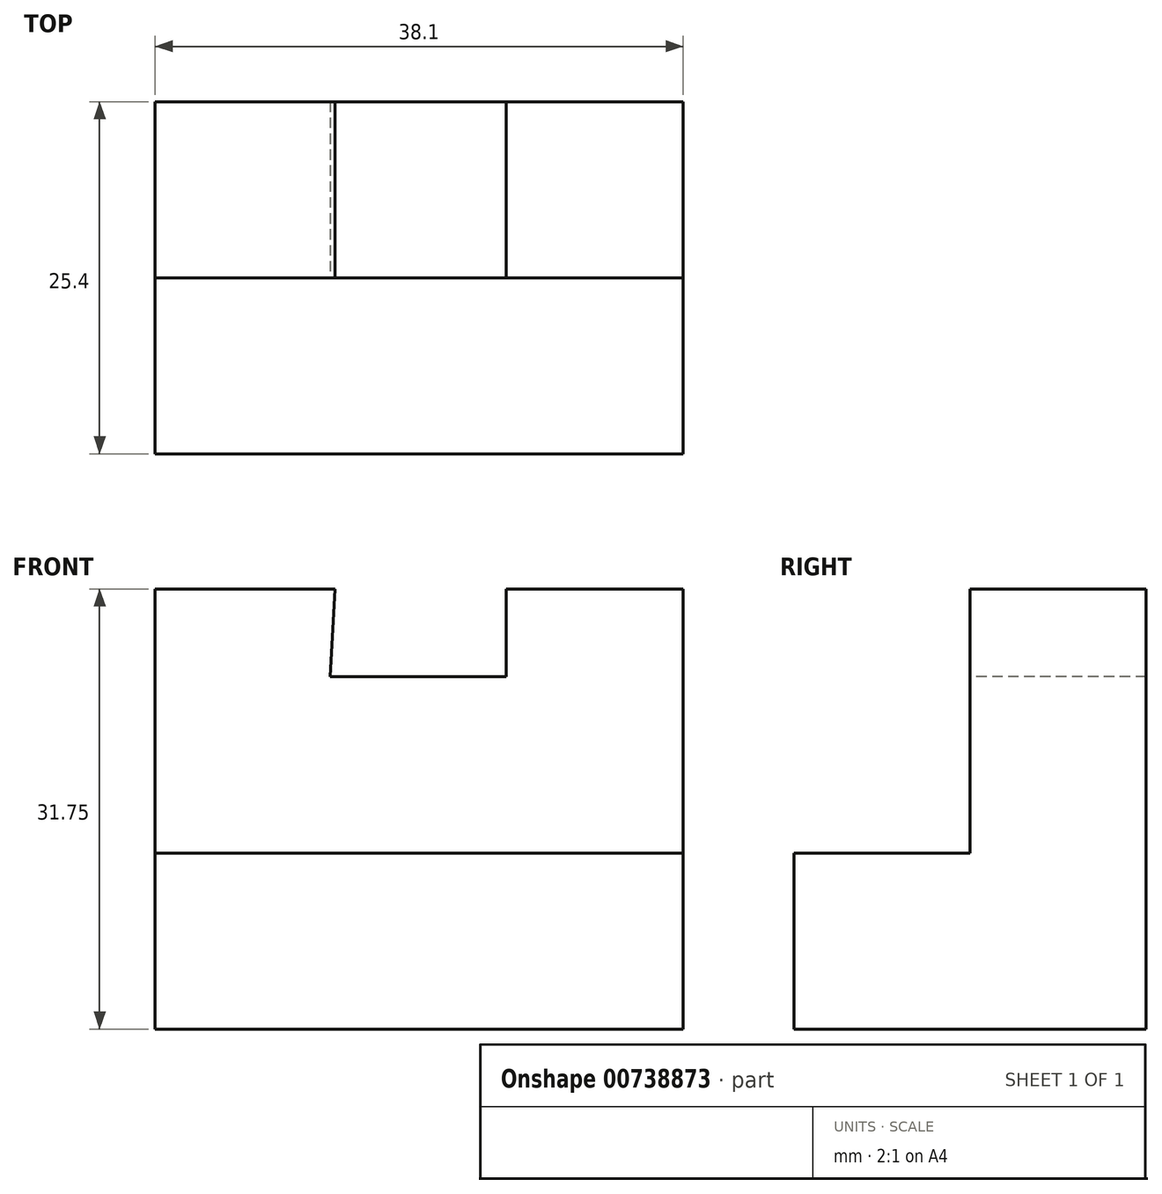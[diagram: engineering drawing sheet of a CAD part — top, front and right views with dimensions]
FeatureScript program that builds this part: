
annotation { "Feature Type Name" : "Feature", "Feature Type Description" : "" }
export const myFeature = defineFeature(function(context is Context, id is Id, definition is map)
    precondition{}
    {
        {
            var Q0;
            Q0=qCreatedBy(makeId("Right.planeOp"),FACE);
            var sketch = newSketch(context, id + "F0", { "sketchPlane" : qUnion([Q0])});
            skLineSegment(sketch, "E0", {"start": v(0, 31.75) * mm, "end": v(0, 0) * mm});
            skLineSegment(sketch, "E1", {"start": v(0, 31.75) * mm, "end": v(-12.7, 31.75) * mm});
            skLineSegment(sketch, "E2", {"start": v(-12.7, 31.75) * mm, "end": v(-12.7, 12.7) * mm});
            skLineSegment(sketch, "E3", {"start": v(-12.7, 12.7) * mm, "end": v(-25.4, 12.7) * mm});
            skLineSegment(sketch, "E4", {"start": v(-25.4, 12.7) * mm, "end": v(-25.4, 0) * mm});
            skLineSegment(sketch, "E5", {"start": v(-25.4, 0) * mm, "end": v(0, 0) * mm});
            skSolve(sketch);
        }
        {
            var Q0;
            Q0 = qSketchRegion(id + "F0", true);
            extrude(context, id + "F1", {"entities" : qUnion([Q0]), "depth" : 38.1 * mm, "offsetDistance" : 25.4 * mm});
        }
        {
            var Q0;
            Q0=makeQuery(id+"F1.opExtrude","SWEPT_FACE",FACE,{"disambiguationData":[OSD([sQuery(id+"F0.wireOp",EDGE,"E2")])]});
            var sketch = newSketch(context, id + "F2", { "sketchPlane" : qUnion([Q0])});
            skLineSegment(sketch, "E6", {"start": v(12.97, 31.75) * mm, "end": v(25.32, 31.75) * mm});
            skLineSegment(sketch, "E7", {"start": v(25.32, 31.75) * mm, "end": v(25.32, 25.4) * mm});
            skLineSegment(sketch, "E8", {"start": v(25.32, 25.4) * mm, "end": v(12.62, 25.4) * mm});
            skLineSegment(sketch, "E9", {"start": v(12.62, 25.4) * mm, "end": v(12.97, 31.75) * mm});
            skSolve(sketch);
        }
        {
            var Q0;
            Q0 = qSketchRegion(id + "F2", true);
            extrude(context, id + "F3", {"entities" : qUnion([Q0]), "operationType" : NewBodyOperationType.REMOVE, "endBound" : BoundingType.THROUGH_ALL, "oppositeDirection" : true, "depth" : 25.4 * mm, "offsetDistance" : 25.4 * mm});
        }
    });
